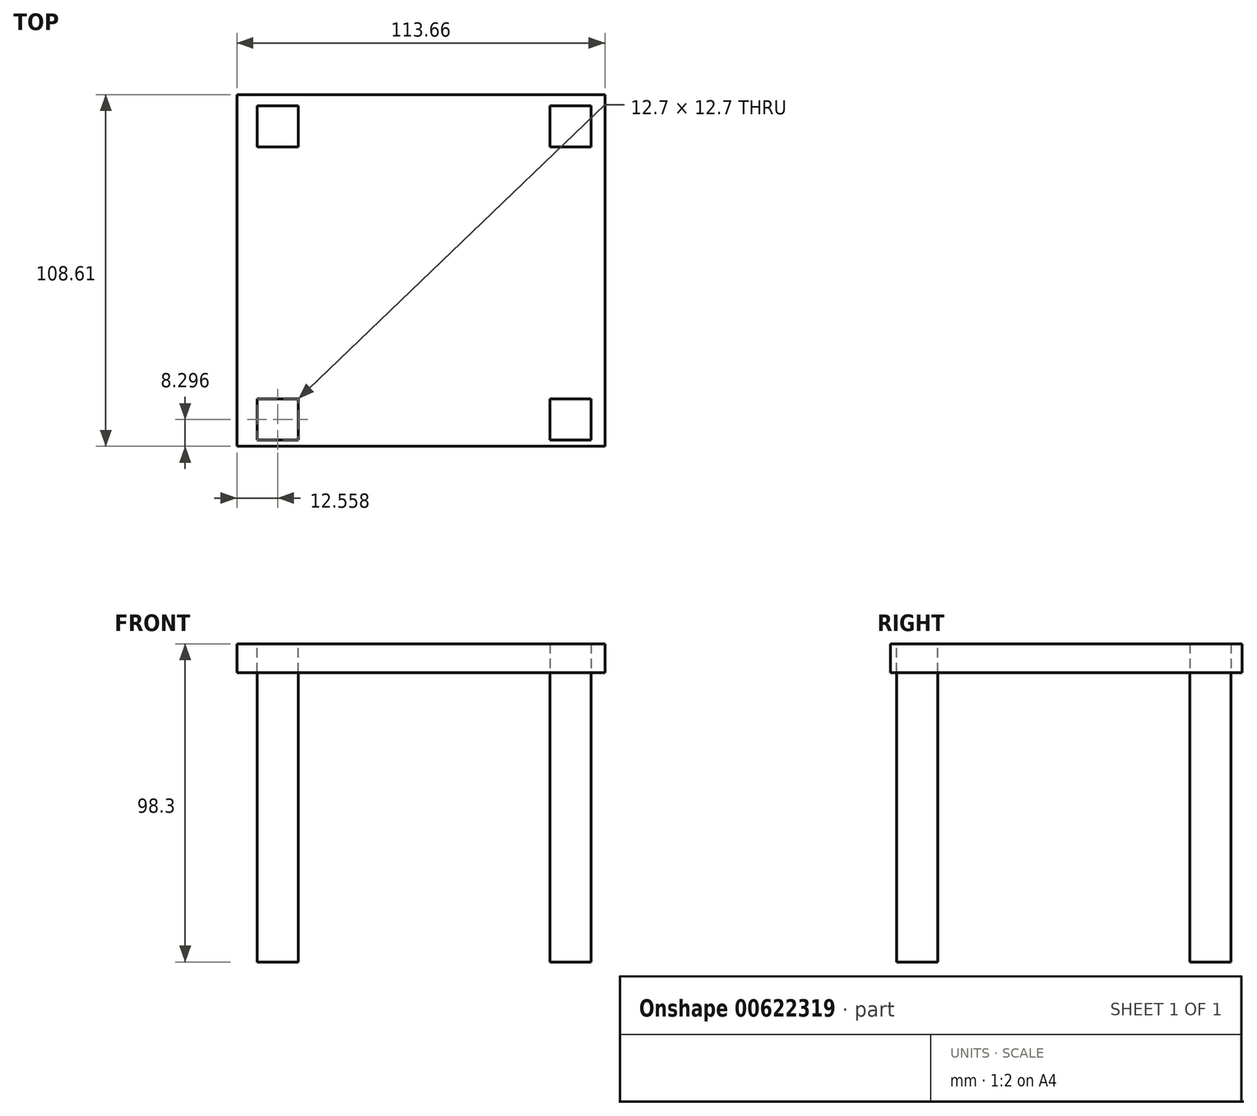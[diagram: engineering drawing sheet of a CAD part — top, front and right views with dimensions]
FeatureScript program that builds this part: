
annotation { "Feature Type Name" : "Feature", "Feature Type Description" : "" }
export const myFeature = defineFeature(function(context is Context, id is Id, definition is map)
    precondition{}
    {
        {
            var Q0;
            Q0=qCreatedBy(makeId("Top.planeOp"),FACE);
            var sketch = newSketch(context, id + "F0", { "sketchPlane" : qUnion([Q0])});
            skLineSegment(sketch, "E0.bottom", {"start": v(-216.75, 63.11) * mm, "end": v(-204.05, 63.11) * mm});
            skLineSegment(sketch, "E0.top", {"start": v(-216.75, 50.41) * mm, "end": v(-204.05, 50.41) * mm});
            skLineSegment(sketch, "E0.left", {"start": v(-216.75, 63.11) * mm, "end": v(-216.75, 50.41) * mm});
            skLineSegment(sketch, "E0.right", {"start": v(-204.05, 63.11) * mm, "end": v(-204.05, 50.41) * mm});
            skLineSegment(sketch, "E1", {"start": v(-255.64, 63.59) * mm, "end": v(-255.64, 14.28) * mm, "construction": true});
            skLineSegment(sketch, "E2.MirrorCS", {"start": v(-294.54, 63.11) * mm, "end": v(-294.54, 50.41) * mm});
            skLineSegment(sketch, "E3.MirrorCS", {"start": v(-294.54, 63.11) * mm, "end": v(-307.24, 63.11) * mm});
            skLineSegment(sketch, "E4.MirrorCS", {"start": v(-307.24, 63.11) * mm, "end": v(-307.24, 50.41) * mm});
            skLineSegment(sketch, "E5.MirrorCS", {"start": v(-294.54, 50.41) * mm, "end": v(-307.24, 50.41) * mm});
            skLineSegment(sketch, "E6", {"start": v(-294.54, 63.11) * mm, "end": v(-216.75, 63.11) * mm});
            skLineSegment(sketch, "E7", {"start": v(-300.9, 11.51) * mm, "end": v(-300.9, 50.41) * mm, "construction": true});
            skPoint(sketch, "E7.startSnap0", {"position": v(-300.9, 50.41) * mm});
            skLineSegment(sketch, "E8", {"start": v(-309.77, 11.51) * mm, "end": v(-204.05, 11.51) * mm, "construction": true});
            skLineSegment(sketch, "E9.MirrorCS", {"start": v(-294.54, -27.38) * mm, "end": v(-307.24, -27.38) * mm});
            skLineSegment(sketch, "E10.MirrorCS", {"start": v(-294.54, -40.08) * mm, "end": v(-294.54, -27.38) * mm});
            skLineSegment(sketch, "E11.MirrorCS", {"start": v(-294.54, -40.08) * mm, "end": v(-307.24, -40.08) * mm});
            skLineSegment(sketch, "E12.MirrorCS", {"start": v(-307.24, -40.08) * mm, "end": v(-307.24, -27.38) * mm});
            skLineSegment(sketch, "E13.MirrorCS", {"start": v(-216.75, -27.38) * mm, "end": v(-204.05, -27.38) * mm});
            skLineSegment(sketch, "E14.MirrorCS", {"start": v(-216.75, -40.08) * mm, "end": v(-216.75, -27.38) * mm});
            skLineSegment(sketch, "E15.MirrorCS", {"start": v(-216.75, -40.08) * mm, "end": v(-204.05, -40.08) * mm});
            skLineSegment(sketch, "E16.MirrorCS", {"start": v(-204.05, -40.08) * mm, "end": v(-204.05, -27.38) * mm});
            skSolve(sketch);
        }
        {
            var Q0;
            Q0=makeQuery(id+"F0.imprint","IMPRINT",FACE,{"disambiguationData":[TD([[makeQuery(id+"F0.imprint","IMPRINT",EDGE,{"derivedFrom":sQuery(id+"F0.wireOp",EDGE,"E13.MirrorCS")}),-1.0]])]});
            var Q1;
            Q1=makeQuery(id+"F0.imprint","IMPRINT",FACE,{"disambiguationData":[TD([[makeQuery(id+"F0.imprint","IMPRINT",EDGE,{"derivedFrom":sQuery(id+"F0.wireOp",EDGE,"E9.MirrorCS")}),1.0]])]});
            var Q2;
            Q2=makeQuery(id+"F0.imprint","IMPRINT",FACE,{"disambiguationData":[TD([[makeQuery(id+"F0.imprint","IMPRINT",EDGE,{"derivedFrom":sQuery(id+"F0.wireOp",EDGE,"E2.MirrorCS")}),-1.0]])]});
            var Q3;
            Q3=makeQuery(id+"F0.imprint","IMPRINT",FACE,{"disambiguationData":[TD([[makeQuery(id+"F0.imprint","IMPRINT",EDGE,{"derivedFrom":sQuery(id+"F0.wireOp",EDGE,"E0.bottom")}),-1.0]])]});
            extrude(context, id + "F1", {"entities" : qUnion([Q0, Q1, Q2, Q3]), "depth" : 98.3 * mm, "offsetDistance" : 25.4 * mm});
        }
        {
            var Q0;
            Q0=makeQuery(id+"F1.opExtrude","CAP_FACE",FACE,{"disambiguationData":[OSD([sQuery(id+"F0.wireOp",EDGE,"E9.MirrorCS"),sQuery(id+"F0.wireOp",EDGE,"E10.MirrorCS"),sQuery(id+"F0.wireOp",EDGE,"E11.MirrorCS"),sQuery(id+"F0.wireOp",EDGE,"E12.MirrorCS")])],"isStart":false});
            var sketch = newSketch(context, id + "F2", { "sketchPlane" : qUnion([Q0])});
            skLineSegment(sketch, "E17.bottom", {"start": v(-313.45, 66.58) * mm, "end": v(-199.79, 66.58) * mm});
            skLineSegment(sketch, "E17.top", {"start": v(-313.45, -42.03) * mm, "end": v(-199.79, -42.03) * mm});
            skLineSegment(sketch, "E17.left", {"start": v(-313.45, 66.58) * mm, "end": v(-313.45, -42.03) * mm});
            skLineSegment(sketch, "E17.right", {"start": v(-199.79, 66.58) * mm, "end": v(-199.79, -42.03) * mm});
            skSolve(sketch);
        }
        {
            var Q0;
            Q0=makeQuery(id+"F2.imprint","IMPRINT",FACE,{"disambiguationData":[TD([[makeQuery(id+"F2.imprint","IMPRINT",EDGE,{"derivedFrom":sQuery(id+"F2.wireOp",EDGE,"E17.bottom")}),-1.0]])]});
            extrude(context, id + "F3", {"entities" : qUnion([Q0]), "oppositeDirection" : true, "depth" : 8.9 * mm, "offsetDistance" : 25.4 * mm});
        }
    });
